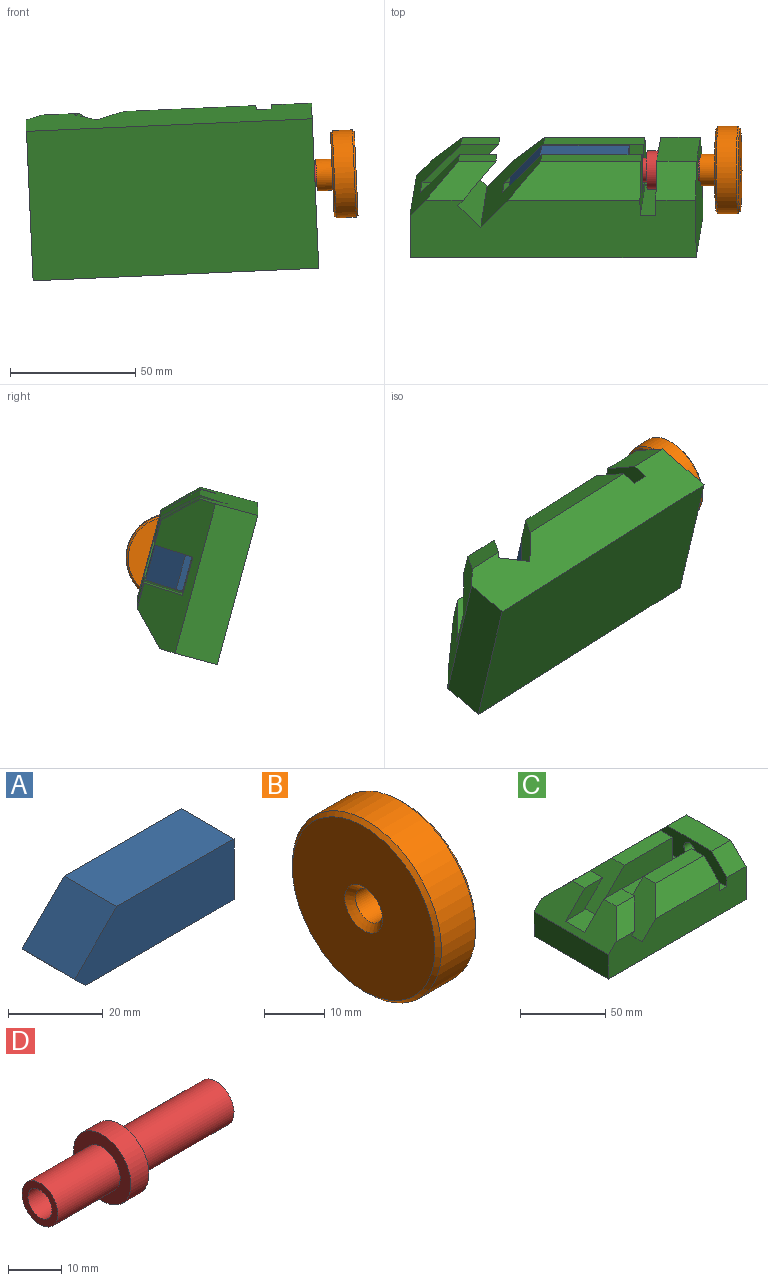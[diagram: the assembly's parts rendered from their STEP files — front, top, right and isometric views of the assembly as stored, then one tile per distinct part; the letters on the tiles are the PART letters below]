
ASSEMBLY  parts=4 mates=3
PART A: 9 faces, bbox 47.6x15.7x15.7 mm
  f0: plane 15.75x3.18mm, normal (-0.71,0,-0.71), area 70.7mm2, adj f1,f4,f5,f6
  f1: plane 44.45x15.75mm, normal (0,0,-1), area 700mm2, adj f0,f2,f5,f6
  f2: plane 15.75x15.75mm, normal (1,0,0), area 176.7mm2, adj f1,f3,f5,f6,f7
  f3: plane 35.05x15.75mm, normal (0,0,1), area 552mm2, adj f2,f4,f5,f6
  f4: plane 15.75x12.57mm, normal (-0.71,0,0.71), area 280mm2, adj f0,f3,f5,f6
  f5: plane 47.63x15.75mm, normal (0,1,0), area 665.9mm2, adj f0,f1,f2,f3,f4
  f6: plane 47.63x15.75mm, normal (0,-1,0), area 665.9mm2, adj f0,f1,f2,f3,f4
  f7: cylinder r=4.76mm len=25.4mm, axis (1,0,0), area 760.1mm2, adj f2,f8
  f8: plane 9.53x9.53mm, normal (1,0,0), area 71.3mm2, adj f7
PART B: 9 faces, bbox 15.9x34.9x34.9 mm
  f0: cylinder r=17.46mm len=34.93mm, axis (1,0,0), area 877.9mm2, adj f7,f8
  f1: plane 33.4x33.4mm, normal (-1,0,0), area 814.1mm2, adj f6,f8
  f2: plane 33.4x33.4mm, normal (1,0,0), area 749.5mm2, adj f3,f7
  f3: cylinder r=6.35mm len=12.7mm, axis (-1,0,0), area 253.4mm2, adj f2,f4
  f4: plane 12.7x12.7mm, normal (1,0,0), area 95mm2, adj f3,f5
  f5: cylinder r=3.17mm len=14.61mm, axis (1,0,0), area 291.4mm2, adj f4,f6
  f6: cone r=4.45mm half-angle=45deg, axis (-1,0,0), area 43mm2, adj f1,f5
  f7: cone r=16.7mm half-angle=45deg, axis (-1,0,0), area 115.7mm2, adj f0,f2
  f8: cone r=17.46mm half-angle=45deg, axis (1,0,0), area 115.7mm2, adj f0,f1
PART C: 31 faces, bbox 114.3x61.9x36.5 mm
  f0: plane 40.08x10.31mm, normal (0,0,1), area 413.3mm2, adj f2,f3,f22,f26
  f1: plane 14.99x10.31mm, normal (0,0,1), area 154.5mm2, adj f5,f20,f24,f28
  f2: plane 61.93x19.05mm, normal (1,0,0), area 766mm2, adj f0,f11,f12,f15,f16,f21,f22,f23
  f3: plane 61.93x23.83mm, normal (-0.71,0,0.71), area 1501.4mm2, adj f0,f4,f12,f15,f16,f21,f22,f23
  f4: plane 61.93x8.98mm, normal (0.71,0,0.71), area 763.3mm2, adj f3,f5,f6,f15,f16,f18,f19,f20
  f5: plane 23.01x14.85mm, normal (0.71,0,-0.71), area 369.1mm2, adj f1,f4,f16,f20,f28
  f6: plane 23.01x14.85mm, normal (0.71,0,-0.71), area 369.1mm2, adj f4,f13,f15,f19,f27
  f7: plane 61.93x17.48mm, normal (-1,0,0), area 1082.2mm2, adj f14,f15,f16,f24
  f8: plane 61.93x36.53mm, normal (1,0,0), area 2029.3mm2, adj f9,f14,f15,f16,f17,f25,f30
  f9: plane 36.53x15.88mm, normal (0,0,1), area 579.8mm2, adj f8,f10,f25,f30
  f10: plane 61.93x19.05mm, normal (-1,0,0), area 947.1mm2, adj f9,f11,f15,f16,f17,f25,f30
  f11: plane 61.93x6.35mm, normal (0,0,1), area 393.2mm2, adj f2,f10,f15,f16
  f12: plane 40.08x10.31mm, normal (0,0,1), area 413.3mm2, adj f2,f3,f21,f29
  f13: plane 14.99x10.31mm, normal (0,0,1), area 154.5mm2, adj f6,f19,f24,f27
  f14: plane 114.3x61.93mm, normal (0,0,-1), area 7078.1mm2, adj f7,f8,f15,f16
  f15: plane 114.3x23.83mm, normal (0,1,0), area 2543.6mm2, adj f2,f3,f4,f6,f7,f8,f10,f11
  f16: plane 114.3x23.83mm, normal (0,-1,0), area 2543.6mm2, adj f2,f3,f4,f5,f7,f8,f10,f11
  f17: cylinder r=4.76mm len=15.88mm, axis (1,0,0), area 475mm2, adj f8,f10
  f18: plane 17.05x15.9mm, normal (0,0,1), area 271mm2, adj f4,f19,f20,f24
  f19: plane 30.86x15.88mm, normal (0,-1,0), area 239mm2, adj f4,f6,f13,f18,f24
  f20: plane 30.86x15.88mm, normal (0,1,0), area 239mm2, adj f1,f4,f5,f18,f24
  f21: plane 55.95x15.88mm, normal (0,1,0), area 762.3mm2, adj f2,f3,f12,f23
  f22: plane 55.95x15.88mm, normal (0,-1,0), area 762.3mm2, adj f0,f2,f3,f23
  f23: plane 55.95x15.9mm, normal (0,0,1), area 889.7mm2, adj f2,f3,f21,f22
  f24: plane 61.93x19.05mm, normal (-0.71,0,0.71), area 1083.2mm2, adj f1,f7,f13,f15,f16,f18,f19,f20
  f25: plane 15.88x12.7mm, normal (0,0.71,0.71), area 285.1mm2, adj f8,f9,f10,f15
  f26: plane 52.78x12.7mm, normal (0,0.71,0.71), area 833.9mm2, adj f0,f2,f3,f15
  f27: plane 27.69x12.7mm, normal (0,0.71,0.71), area 269.2mm2, adj f6,f13,f15,f24
  f28: plane 27.69x12.7mm, normal (0,-0.71,0.71), area 269.2mm2, adj f1,f5,f16,f24
  f29: plane 52.78x12.7mm, normal (0,-0.71,0.71), area 833.9mm2, adj f2,f3,f12,f16
  f30: plane 15.88x12.7mm, normal (0,-0.71,0.71), area 285.1mm2, adj f8,f9,f10,f16
PART D: 9 faces, bbox 46.7x15.2x15.2 mm
  f0: cylinder r=4.76mm len=16.51mm, axis (-1,0,0), area 494mm2, adj f1,f4
  f1: plane 9.53x9.53mm, normal (-1,0,0), area 39.6mm2, adj f0,f7
  f2: cylinder r=7.62mm len=15.24mm, axis (-1,0,0), area 228.6mm2, adj f3,f4
  f3: plane 15.24x15.24mm, normal (1,0,0), area 111.2mm2, adj f2,f5
  f4: plane 15.24x15.24mm, normal (-1,0,0), area 111.2mm2, adj f0,f2
  f5: cylinder r=4.76mm len=25.4mm, axis (-1,0,0), area 760.1mm2, adj f3,f6
  f6: plane 9.53x9.53mm, normal (1,0,0), area 71.3mm2, adj f5
  f7: cylinder r=3.17mm len=12.7mm, axis (-1,0,0), area 253.4mm2, adj f1,f8
  f8: plane 6.35x6.35mm, normal (-1,0,0), area 31.7mm2, adj f7
PLACE A rot(axis=(-1,-0.03,-0.02),74.9deg) t=(63.17,-29.61,38.95)mm
PLACE B rot(axis=(-0.02,0,1),180deg) t=(146.01,-19.95,37.06)mm
PLACE C rot(axis=(-1,-0.03,-0.02),74.9deg) t=(23.76,-55.06,54.26)mm
PLACE D rot(axis=(0,1,0),177.5deg) t=(139.67,-19.95,36.78)mm
MATE cylindrical D.f5 <-> A.f7  axis (1,0,0.04) through (105.71,-19.95,35.28)mm
MATE slider A.f1 <-> C.f23  axis (0.01,-0.97,-0.26) through (88.88,-27.55,32.48)mm
MATE fastened B.f3 <-> D.f7  axis (-1,0,-0.04) through (139.67,-19.95,36.78)mm
